# Revit family: Haworth_Masters_Credenza_Desk
name_source: partatom
category: Furniture Systems
units: mm (PartAtom-declared; Revit-internal decimal feet)

## family parameters
Always vertical = Yes
Cut with Voids When Loaded = No
OmniClass Number = 23.40.70.14.64.21
OmniClass Title = Systems Furniture
Part Type = Normal
Room Calculation Point = No
Round Connector Dimension = Use Diameter
Shared = No
Work Plane-Based = No

## types (18) — shared parameters
Actual Height = 29"
Assembly Code = E2020200
Cabinet Finish = Haworth _ Wood _ Wenge
Custom Size = No
Default Elevation = 0"
Description = Masters Credenza Desk
Height = 29"
Height Range = 28 11/16-47 3/16 in.
Leg Finish = Haworth _ Paint _ Metallic Champagne
Manufacturer = Haworth
Max. Depth = 28"
Max. Height = 47 3/16"
Max. Width = 96"
Min. Depth = 22"
Min. Height = 28 11/16"
Min. Width = 58"
Min/Max Depth = 22, 28 in.
Min/Max Width = 68-70 in. @ 6 in. Increments
Model = Masters
Modesty Panel Finish = Haworth _ Wood _ White Oak
Revision Number = 0
Size = Verify Final Dim. w/ Haworth
Support Height = 27 13/16"
Support Offset = 1 1/4"
Sustainability Info = http://media.haworth.com
Top = Yes
URL = http://www.haworth.com
URL - Product = http://www.haworth.com
Warranty = http://www.haworth.com
Worksurface Thickness = 1 3/16"

## per-type parameters (varying)
| type | Actual Depth | Actual Support Depth | Actual Width | Depth | Left Shroud | Modesty Shroud | Right Shroud | Width |
| 22d 58w - Credenza Desk | 22" | 19 1/2" | 58" | 22" | No | No | No | 58" |
| 22d 64w - Credenza Desk | 22" | 19 1/2" | 64" | 22" | No | No | No | 64" |
| 22d 70w - Credenza Desk | 22" | 19 1/2" | 70" | 22" | No | No | No | 70" |
| 28d 58w - Credenza Desk | 28" | 25 1/2" | 58" | 28" | No | No | No | 58" |
| 28d 64w - Credenza Desk | 28" | 25 1/2" | 64" | 28" | No | No | No | 64" |
| 28d 70w - Credenza Desk | 28" | 25 1/2" | 70" | 28" | No | No | No | 70" |
| 22d 58w - Credenza Desk - With Shroud | 22" | 19 1/2" | 58" | 22" | Yes | No | Yes | 58" |
| 22d 64w - Credenza Desk - With Shroud | 22" | 19 1/2" | 64" | 22" | Yes | No | Yes | 64" |
| 22d 70w - Credenza Desk - With Shroud | 22" | 19 1/2" | 70" | 22" | Yes | No | Yes | 70" |
| 28d 58w - Credenza Desk - With Shroud | 28" | 25 1/2" | 58" | 28" | Yes | No | Yes | 58" |
| 28d 64w - Credenza Desk - With Shroud | 28" | 25 1/2" | 64" | 28" | Yes | No | Yes | 64" |
| 28d 70w - Credenza Desk - With Shroud | 28" | 25 1/2" | 70" | 28" | Yes | No | Yes | 70" |
| 22d 58w - Credenza Desk - With Shroud and Modesty Panel | 22" | 19 1/2" | 58" | 22" | Yes | Yes | Yes | 58" |
| 22d 64w - Credenza Desk - With Shroud and Modesty Panel | 22" | 19 1/2" | 64" | 22" | Yes | Yes | Yes | 64" |
| 22d 70w - Credenza Desk - With Shroud and Modesty Panel | 22" | 19 1/2" | 70" | 22" | Yes | Yes | Yes | 70" |
| 28d 58w - Credenza Desk - With Shroud and Modesty Panel | 28" | 25 1/2" | 58" | 28" | Yes | Yes | Yes | 58" |
| 28d 64w - Credenza Desk - With Shroud and Modesty Panel | 28" | 25 1/2" | 64" | 28" | Yes | Yes | Yes | 64" |
| 28d 70w - Credenza Desk - With Shroud and Modesty Panel | 28" | 25 1/2" | 70" | 28" | Yes | Yes | Yes | 70" |

## geometry (parser evidence)
native form markers: Blend x4, Sweep x16
no freeform markers — native parametric forms only
